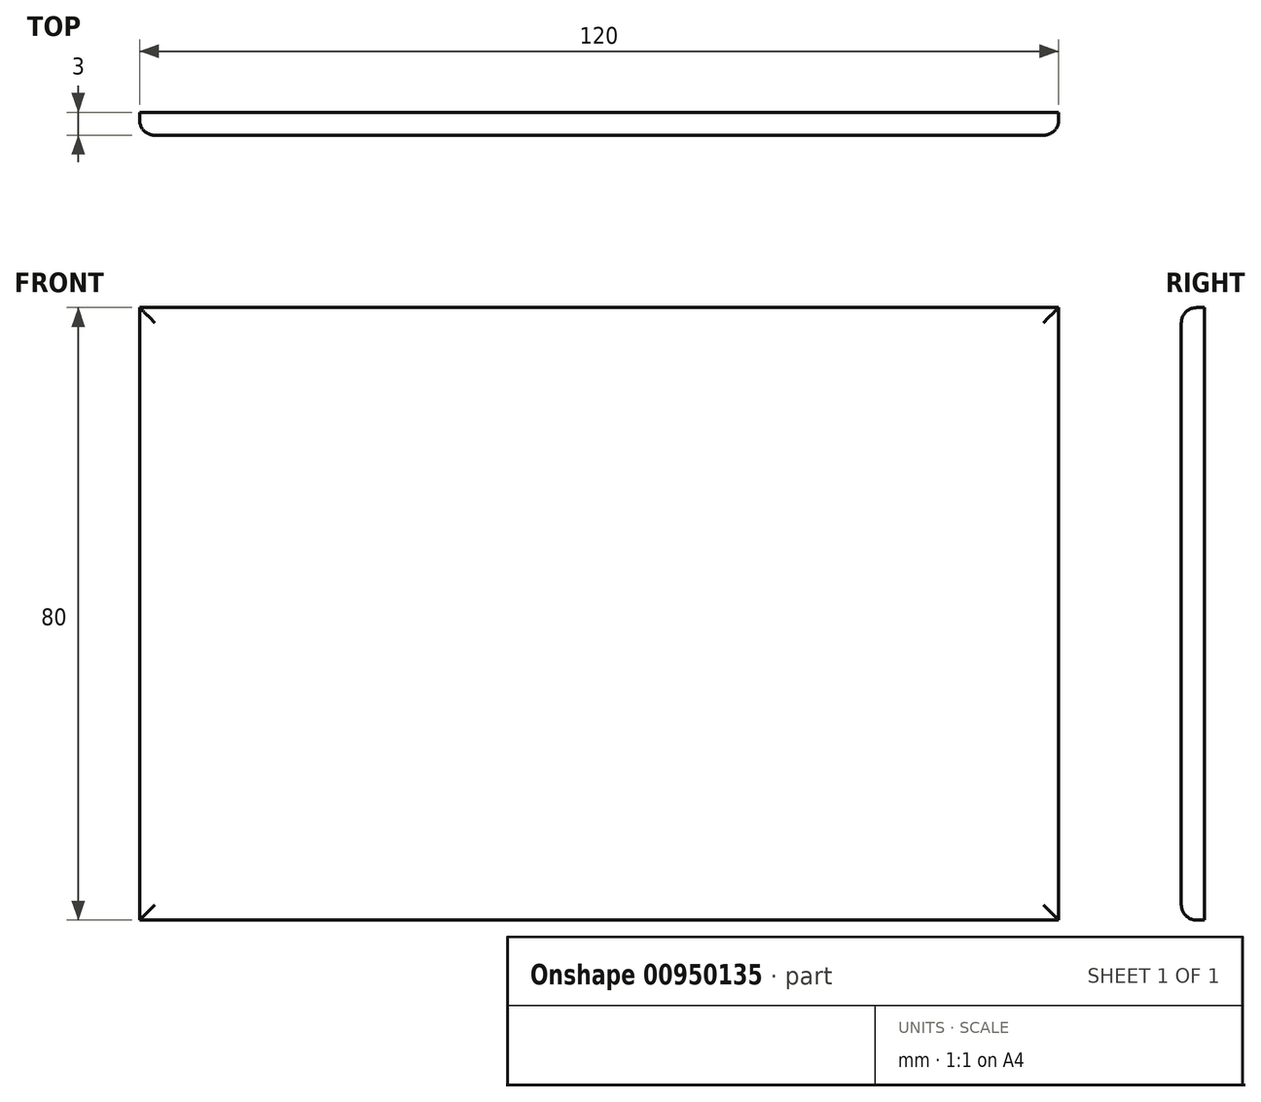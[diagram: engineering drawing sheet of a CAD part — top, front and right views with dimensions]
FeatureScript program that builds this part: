
annotation { "Feature Type Name" : "Feature", "Feature Type Description" : "" }
export const myFeature = defineFeature(function(context is Context, id is Id, definition is map)
    precondition{}
    {
        {
            var Q0;
            Q0=qCreatedBy(makeId("Front.planeOp"),FACE);
            var sketch = newSketch(context, id + "F0", { "sketchPlane" : qUnion([Q0])});
            skLineSegment(sketch, "E0.bottom", {"start": v(60, 40) * mm, "end": v(-60, 40) * mm});
            skLineSegment(sketch, "E0.top", {"start": v(60, -40) * mm, "end": v(-60, -40) * mm});
            skLineSegment(sketch, "E0.left", {"start": v(60, 40) * mm, "end": v(60, -40) * mm});
            skLineSegment(sketch, "E0.right", {"start": v(-60, 40) * mm, "end": v(-60, -40) * mm});
            skPoint(sketch, "E0.middle", {"position": v(0, 0) * mm});
            skSolve(sketch);
        }
        {
            var Q0;
            Q0=makeQuery(id+"F0.imprint","IMPRINT",FACE,{"disambiguationData":[TD([[makeQuery(id+"F0.imprint","IMPRINT",EDGE,{"derivedFrom":sQuery(id+"F0.wireOp",EDGE,"E0.bottom")}),1.0]])]});
            extrude(context, id + "F1", {"entities" : qUnion([Q0]), "depth" : 3 * mm, "offsetDistance" : 25 * mm});
        }
        {
            var Q0;
            Q0=makeQuery(id+"F1.opExtrude","CAP_EDGE",EDGE,{"disambiguationData":[OSD([sQuery(id+"F0.wireOp",EDGE,"E0.bottom")])],"isStart":false});
            var Q1;
            Q1=makeQuery(id+"F1.opExtrude","CAP_EDGE",EDGE,{"disambiguationData":[OSD([sQuery(id+"F0.wireOp",EDGE,"E0.right")])],"isStart":false});
            var Q2;
            Q2=makeQuery(id+"F1.opExtrude","CAP_EDGE",EDGE,{"disambiguationData":[OSD([sQuery(id+"F0.wireOp",EDGE,"E0.top")])],"isStart":false});
            var Q3;
            Q3=makeQuery(id+"F1.opExtrude","CAP_EDGE",EDGE,{"disambiguationData":[OSD([sQuery(id+"F0.wireOp",EDGE,"E0.left")])],"isStart":false});
            fillet(context, id + "F2", {"entities" : qUnion([Q0, Q1, Q2, Q3]), "radius" : 2 * mm, "tangentPropagation" : true, "allowEdgeOverflow" : false});
        }
    });
